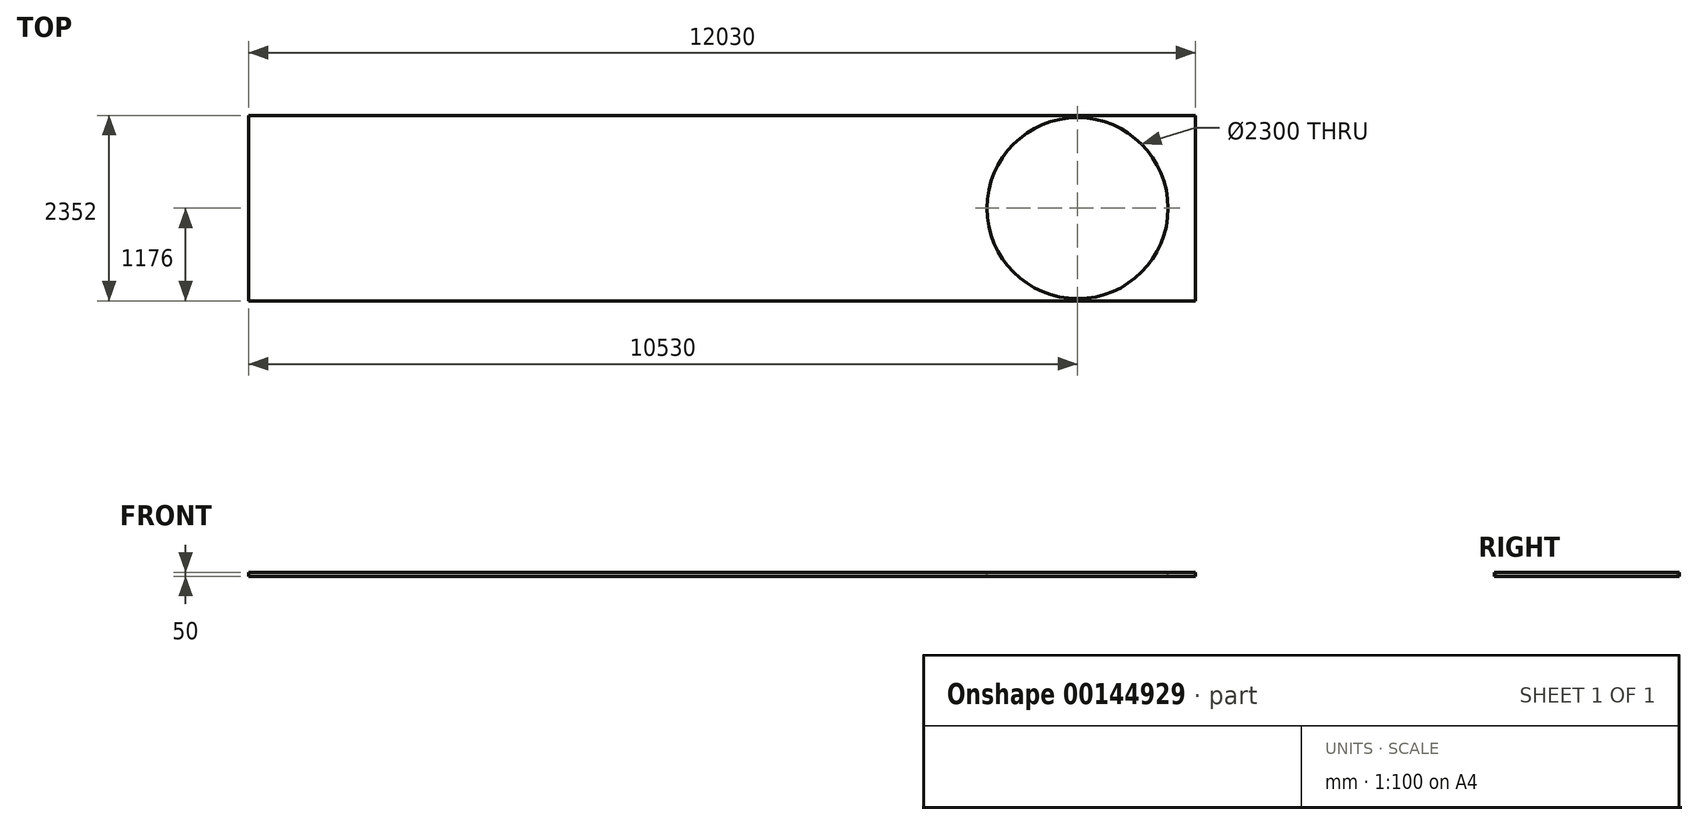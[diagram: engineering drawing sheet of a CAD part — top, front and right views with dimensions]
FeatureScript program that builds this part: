
annotation { "Feature Type Name" : "Feature", "Feature Type Description" : "" }
export const myFeature = defineFeature(function(context is Context, id is Id, definition is map)
    precondition{}
    {
        {
            var Q0;
            Q0=qCreatedBy(makeId("Top.planeOp"),FACE);
            var sketch = newSketch(context, id + "F0", { "sketchPlane" : qUnion([Q0])});
            skLineSegment(sketch, "E0.bottom", {"start": v(6015, -1176) * mm, "end": v(-6015, -1176) * mm});
            skLineSegment(sketch, "E0.top", {"start": v(6015, 1176) * mm, "end": v(-6015, 1176) * mm});
            skLineSegment(sketch, "E0.left", {"start": v(6015, -1176) * mm, "end": v(6015, 1176) * mm});
            skLineSegment(sketch, "E0.right", {"start": v(-6015, -1176) * mm, "end": v(-6015, 1176) * mm});
            skPoint(sketch, "E0.middle", {"position": v(0, 0) * mm});
            skSolve(sketch);
        }
        {
            var Q0;
            Q0=makeQuery(id+"F0.imprint","IMPRINT",FACE,{"disambiguationData":[TD([[makeQuery(id+"F0.imprint","IMPRINT",EDGE,{"derivedFrom":sQuery(id+"F0.wireOp",EDGE,"E0.bottom")}),-1.0]])]});
            extrude(context, id + "F4", {"entities" : qUnion([Q0]), "depth" : 50 * mm});
        }
        {
            var Q0;
            Q0=qCreatedBy(makeId("Top.planeOp"),FACE);
            var sketch = newSketch(context, id + "F1", { "sketchPlane" : qUnion([Q0])});
            skLineSegment(sketch, "E1.bottom", {"start": v(6015, -2005.58) * mm, "end": v(-6015, -2005.58) * mm});
            skLineSegment(sketch, "E1.top", {"start": v(6015, 2005.58) * mm, "end": v(-6015, 2005.58) * mm});
            skLineSegment(sketch, "E1.left", {"start": v(6015, -2005.58) * mm, "end": v(6015, 2005.58) * mm});
            skLineSegment(sketch, "E1.right", {"start": v(-6015, -2005.58) * mm, "end": v(-6015, 2005.58) * mm});
            skPoint(sketch, "E1.middle", {"position": v(0, 0) * mm});
            skSolve(sketch);
        }
        {
            var Q0;
            Q0=makeQuery(id+"F4.opExtrude","CAP_FACE",FACE,{"disambiguationData":[OSD([sQuery(id+"F0.wireOp",EDGE,"E0.bottom"),sQuery(id+"F0.wireOp",EDGE,"E0.top"),sQuery(id+"F0.wireOp",EDGE,"E0.left"),sQuery(id+"F0.wireOp",EDGE,"E0.right")])],"isStart":false});
            var sketch = newSketch(context, id + "F2", { "sketchPlane" : qUnion([Q0])});
            skCircle(sketch, "E2", {"center": v(4515, 0) * mm, "radius": 1150 * mm});
            skSolve(sketch);
        }
        {
            var Q0;
            Q0=makeQuery(id+"F2.imprint","IMPRINT",FACE,{"disambiguationData":[TD([[makeQuery(id+"F2.imprint","IMPRINT",EDGE,{"derivedFrom":sQuery(id+"F2.wireOp",EDGE,"E2")}),1.0]])]});
            extrude(context, id + "F3", {"entities" : qUnion([Q0]), "operationType" : NewBodyOperationType.REMOVE, "endBound" : BoundingType.THROUGH_ALL, "oppositeDirection" : true, "depth" : 25 * mm});
        }
    });
